# Revit family: Hager-Univers-IP55-D275-H2050-Cl.II-Steel_encl-CH-de
name_source: partatom
category: Equipement électrique
units: mm (PartAtom-declared; Revit-internal decimal feet)

## family parameters
Configuration du panneau = Deux colonnes, circuits au sein
Cote de connecteur circulaire = Utiliser le diamètre
Couper avec des vides une fois chargée = Non
Hôte = Face
Partagée = Non
Point de calcul de pièce = Non
Type d'élément = Tableau de raccordement

## types (11) — shared parameters
Commentaires du type = Univers
EF000003 - Montageart = EV012274 - Bodenaufstellung
EF000007 - Farbe = EV000270 - grau
EF000040 - Höhe = 2050 mm  [stored 6.72572 ft]
EF000049 - Tiefe = 275 mm  [stored 0.902231 ft]
EF000116 - RAL-Nummer = 7035
EF000118 - Mit Montageplatte = Non
EF000266 - Anzahl der Reihen = 12
EF000339 - Art der Abdeckung = EV004216 - Tür
EF001088 - Anbaumöglichkeit = Oui
EF001131 - Innentiefe = 275 mm  [stored 0.902231 ft]
EF001596 - Werkstoff des Gehäuses = EV000179 - Stahl
EF001613 - Funktionserhalt = EV000494 - ohne
EF002950 - Breite in Teilungseinheiten = 24
EF003532 - Geeignet für Außengebrauch = Non
EF004293 - Schlagfestigkeit = EV008784 - IK10
EF005474 - Schutzart (IP) = EV006420 - IP55
EF006306 - Mit Schloss = Non
EF007800 - Geeignet für Blitzschutz = Non
EF008873 - Nennstrom (In) = 800 A
EF009170 - Materialstärke Gehäuse = 2 mm  [stored 0.00656168 ft]
EF009171 - Materialstärke Tür/Deckel = 2 mm  [stored 0.00656168 ft]
EF009212 - Ausführung Deckel = EV000116 - geschlossen
EF015940 - Deckel mit Überdruckentlastung = Non
Fabricant = Hager
HG000002 - Mit tür = Oui
HG000003 - Bereich = Univers
HG000006 - Unterputz = Non
HG000023 - Gehäuse mit doppeltem Querschnitt = Non
HG000024 - Höhe des unteren Teils = 800 mm  [stored 2.62467 ft]
HG000026 - Stehend auf dem Boden = Oui
HG000027 - Sockelhöhe = 200 mm  [stored 0.656168 ft]
zero-valued in all types: EF000218 - Einbautiefe, Elévation par défaut

## per-type parameters (varying)
| type | EF000008 - Breite | EF000437 - Anzahl der Leitungseinführungen | EF004427 - Anzahl der Module | EF004464 - Art der Tür | EF006244 - Transparenter Deckel/Tür | EF009554 - Anzahl der Öffnungen für Flanschplatten | HG000004 - Herstellerreferenz | HG000009 - Doppelflügeligen Tür | HG000010 - Asymmetrische Türen |
| Bodenaufstellung IP55 B1050 H2050 T275  - FR24L2 | 1050 mm | 8 | 576 | EV003602 - Doppel | Oui | 8 | FR24L2 | Oui | Oui |
| Bodenaufstellung IP55 B1050 H2050 T275  - FR24S2 | 1050 mm | 8 | 576 | EV003602 - Doppel | Non | 8 | FR24S2 | Oui | Oui |
| Bodenaufstellung IP55 B1300 H2050 T275  - FR25L2 | 1300 mm  [stored 4.26509 ft] | 10 | 720 | EV003602 - Doppel | Oui | 10 | FR25L2 | Oui | Oui |
| Bodenaufstellung IP55 B1300 H2050 T275  - FR25S2 | 1300 mm  [stored 4.26509 ft] | 10 | 720 | EV003602 - Doppel | Non | 10 | FR25S2 | Oui | Oui |
| Bodenaufstellung IP55 B1550 H2050 T275  - FR26L2 | 1550 mm  [stored 5.0853 ft] | 12 | 864 | EV003602 - Doppel | Oui | 12 | FR26L2 | Oui | Oui |
| Bodenaufstellung IP55 B1550 H2050 T275  - FR26S2 | 1550 mm  [stored 5.0853 ft] | 12 | 864 | EV003602 - Doppel | Non | 12 | FR26S2 | Oui | Oui |
| Bodenaufstellung IP55 B300 H2050 T275  - FR21S2 | 300 mm | 2 | 144 | EV002646 - Einzel | Non | 2 | FR21S2 | Non | Non |
| Bodenaufstellung IP55 B550 H2050 T275  - FR22L2 | 550 mm | 4 | 288 | EV002646 - Einzel | Oui | 4 | FR22L2 | Non | Non |
| Bodenaufstellung IP55 B550 H2050 T275  - FR22S2 | 550 mm | 4 | 288 | EV002646 - Einzel | Non | 4 | FR22S2 | Non | Non |
| Bodenaufstellung IP55 B800 H2050 T275  - FR23L2 | 800 mm  [stored 2.62467 ft] | 6 | 432 | EV002646 - Einzel | Oui | 6 | FR23L2 | Non | Non |
| Bodenaufstellung IP55 B800 H2050 T275  - FR23S2 | 800 mm  [stored 2.62467 ft] | 6 | 432 | EV002646 - Einzel | Non | 6 | FR23S2 | Non | Non |

note: [stored X ft] marks values corroborated as IEEE doubles in the binary element streams (Revit-internal decimal feet)

## geometry (parser evidence)
native form markers: Sweep x10
no freeform markers — native parametric forms only
